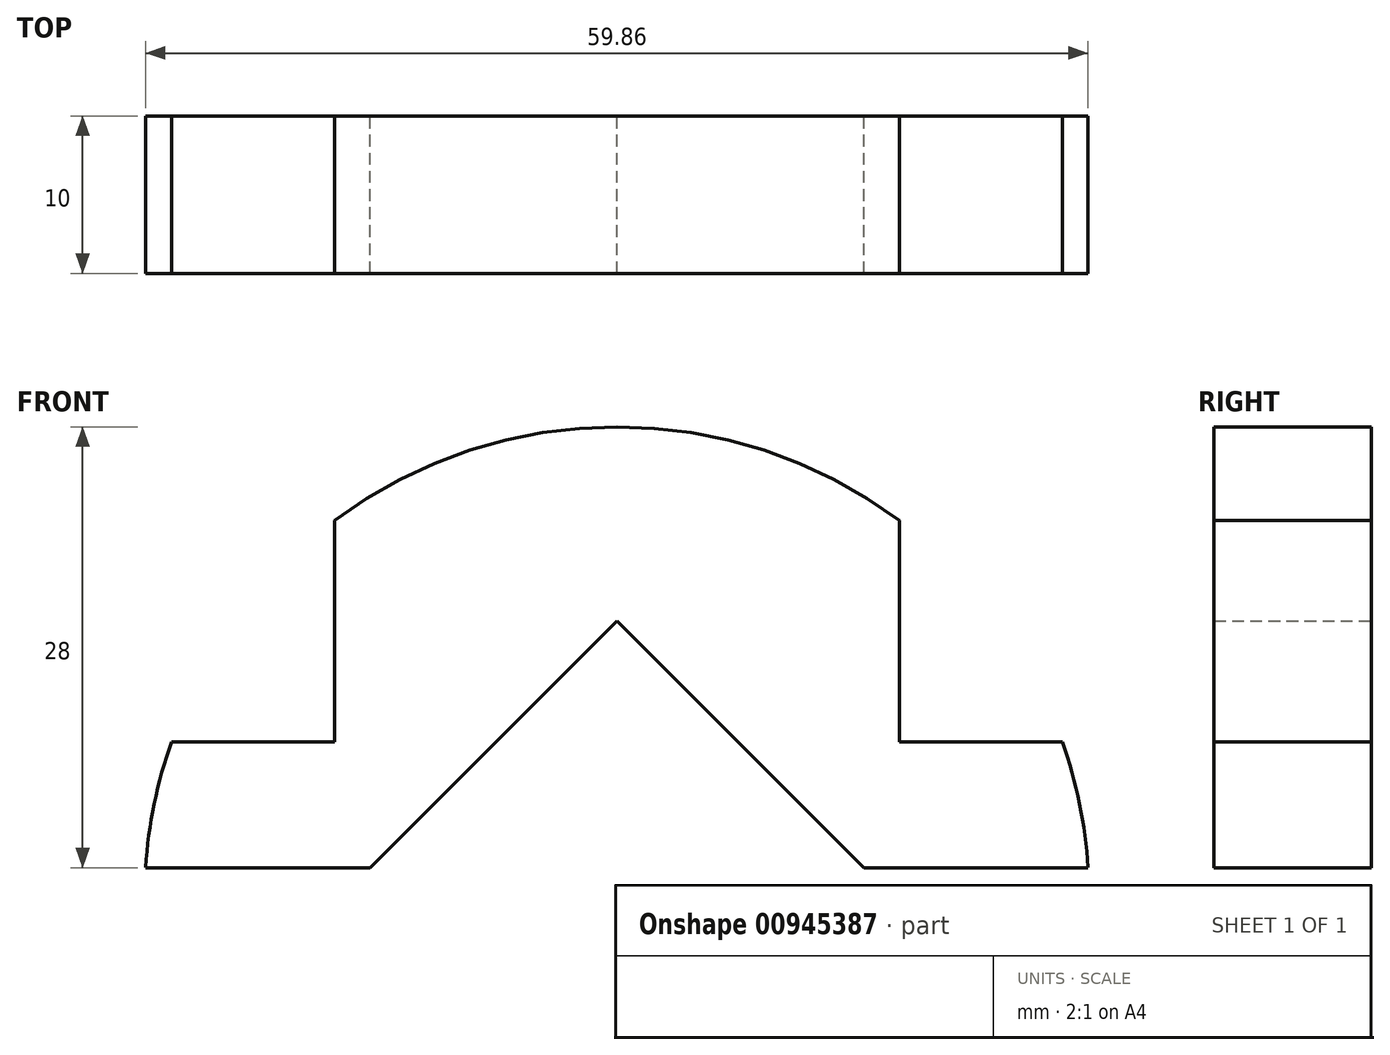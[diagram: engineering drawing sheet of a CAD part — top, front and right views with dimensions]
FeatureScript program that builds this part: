
annotation { "Feature Type Name" : "Feature", "Feature Type Description" : "" }
export const myFeature = defineFeature(function(context is Context, id is Id, definition is map)
    precondition{}
    {
        {
            var Q0;
            Q0=qCreatedBy(makeId("Front.planeOp"),FACE);
            var sketch = newSketch(context, id + "F0", { "sketchPlane" : qUnion([Q0])});
            skLineSegment(sketch, "E0", {"start": v(-17.68, 0) * mm, "end": v(0, 17.68) * mm, "construction": true});
            skLineSegment(sketch, "E1.MirrorCS", {"start": v(17.68, 0) * mm, "end": v(0, 17.68) * mm, "construction": true});
            skLineSegment(sketch, "E2", {"start": v(0, 17.68) * mm, "end": v(-15.68, 2) * mm});
            skLineSegment(sketch, "E3", {"start": v(-15.68, 2) * mm, "end": v(-29.93, 2) * mm});
            skLineSegment(sketch, "E4", {"start": v(-29.93, 2) * mm, "end": v(-29.93, 26.96) * mm, "construction": true});
            skArc(sketch, "E5", {"start": v(0, 30) * mm, "mid": v(-20.5, 21.9) * mm, "end": v(-29.93, 2) * mm});
            skLineSegment(sketch, "E6.bottom", {"start": v(-19.93, 27.35) * mm, "end": v(-25.93, 27.35) * mm, "construction": true});
            skLineSegment(sketch, "E6.top", {"start": v(-19.93, -28.56) * mm, "end": v(-25.93, -28.56) * mm, "construction": true});
            skLineSegment(sketch, "E6.left", {"start": v(-19.93, 27.35) * mm, "end": v(-19.93, -28.56) * mm, "construction": true});
            skLineSegment(sketch, "E6.right", {"start": v(-25.93, 27.35) * mm, "end": v(-25.93, -28.56) * mm, "construction": true});
            skLineSegment(sketch, "E7", {"start": v(-17.93, 10) * mm, "end": v(-28.28, 10) * mm});
            skLineSegment(sketch, "E8", {"start": v(-17.93, 10) * mm, "end": v(-17.93, 24.05) * mm});
            skLineSegment(sketch, "E9", {"start": v(0, 0) * mm, "end": v(0, 38.25) * mm, "construction": true});
            skArc(sketch, "E10.MirrorCS", {"start": v(0, 30) * mm, "mid": v(20.5, 21.9) * mm, "end": v(29.93, 2) * mm});
            skLineSegment(sketch, "E11.MirrorCS", {"start": v(17.93, 10) * mm, "end": v(17.93, 24.05) * mm});
            skLineSegment(sketch, "E12.MirrorCS", {"start": v(17.93, 10) * mm, "end": v(28.28, 10) * mm});
            skLineSegment(sketch, "E13.MirrorCS", {"start": v(15.68, 2) * mm, "end": v(29.93, 2) * mm});
            skLineSegment(sketch, "E14.MirrorCS", {"start": v(0, 17.68) * mm, "end": v(15.68, 2) * mm});
            skSolve(sketch);
        }
        {
            var Q0;
            Q0=makeQuery(id+"F0.imprint","IMPRINT",FACE,{"disambiguationData":[TD([[makeQuery(id+"F0.imprint","IMPRINT",EDGE,{"derivedFrom":sQuery(id+"F0.wireOp",EDGE,"E2")}),-1.0]])]});
            extrude(context, id + "F1", {"entities" : qUnion([Q0]), "depth" : 10 * mm, "offsetDistance" : 25 * mm});
        }
    });
